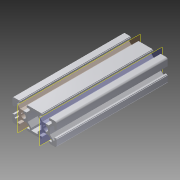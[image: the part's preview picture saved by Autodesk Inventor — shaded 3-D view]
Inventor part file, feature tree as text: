
AUTODESK INVENTOR PART (.ipt)
format: ipt  version: 2015 SP1 (Build 190203100, 203)  size: 309,248 bytes
history: native  units: mm
features: extrude x5, mirror x4, sketch x3, plane x2, fillet x1, projected_geometry x1
ambient origin geometry x8: Origin, YZ Plane, XZ Plane, XY Plane, X Axis, Y Axis, Z Axis, Center Point
bodies: Solid1 (feature_tree)
feature tree (16):
  extrude  "Extrusion1"  Depth=10.0mm
  fillet  "Fillet1"  Radius=10.0mm
  mirror  "Mirror1"
  mirror  "Mirror2"
  extrude  "Extrusion2"  Depth=6.1mm
  mirror  "Mirror3"
  sketch  "Sketch3"  dims[d6=1.5mm d7=2.0mm d8=100.0mm d9=0.0mm d10=1.5mm d11=3.6mm d12=4.45mm d13=10.0mm d14=0.0mm d15=1.5mm d16=10.0mm d17=0.0mm d18=10.0mm d19=0.0mm d20=10.0mm d21=0.0mm]
  extrude  "Extrusion3"  Depth=2.0mm
  extrude  "Extrusion4"  Depth=100.0mm TaperAngle=0.0deg
  mirror  "Mirror4"
  extrude  "Extrusion5"  Depth=1.5mm
  plane  "Work Plane1"
  plane  "Work Plane2"
  sketch  "Sketch1"  dims[d0=45.0deg d1=5.63mm d2=10.0mm]
  sketch  "Sketch2"  dims[d3=3.1mm d5=6.1mm]
  projected_geometry  "Projected Loop1"
